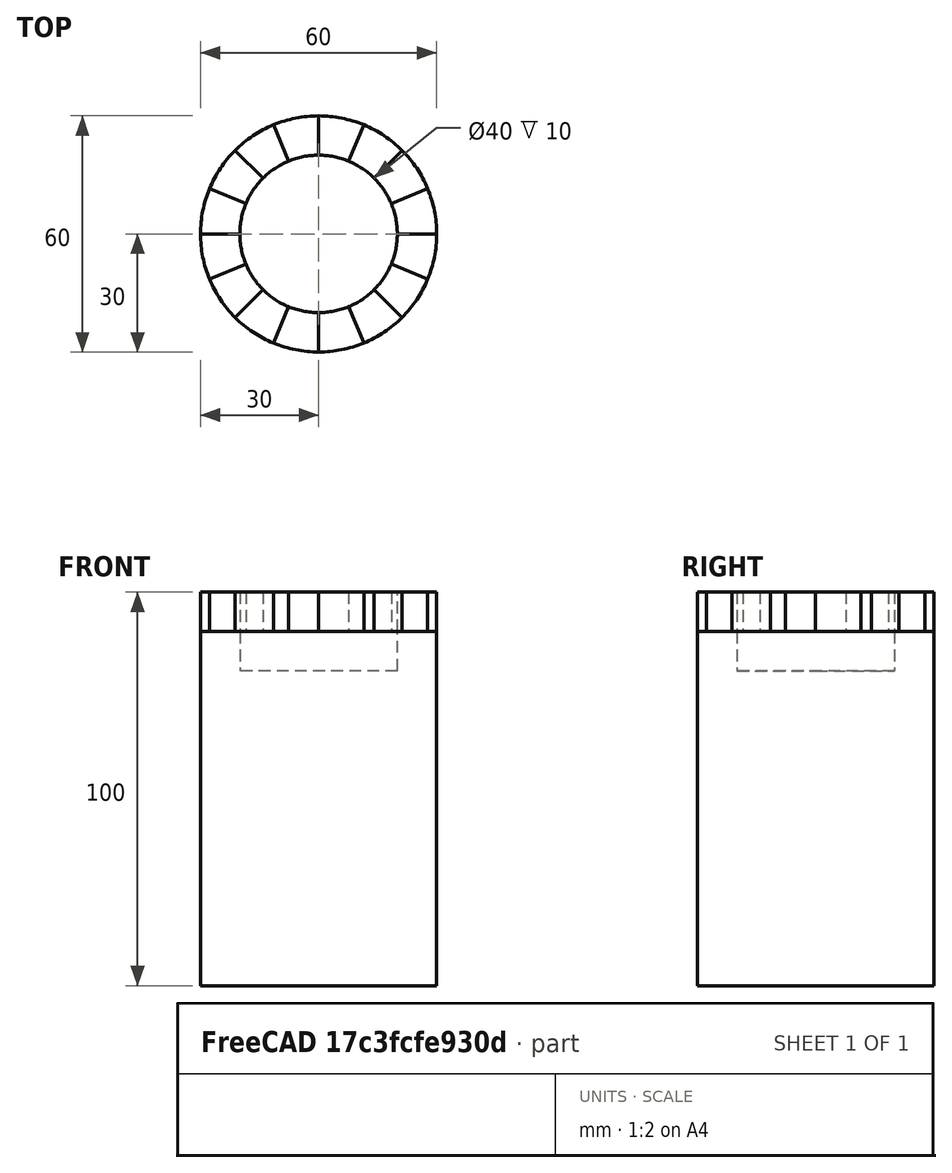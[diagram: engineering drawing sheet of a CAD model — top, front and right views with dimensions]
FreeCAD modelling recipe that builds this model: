
FCSTD DOCUMENT  (FreeCAD 0.21R33694 (Git))
Label: OJT1_T11R03_castillo
License: All rights reserved
LicenseURL: http://en.wikipedia.org/wiki/All_rights_reserved
objects: Part::Cylinder×11, Part::Cut×9
note: 20 computed .brp shape members not serialized (recipe doc carries the construction recipe); baked Part::Feature solids carry a one-line shape summary decoded from their .brp

FEATURE [Part::Cylinder] Cylinder
  Angle = 360
  AttacherType = Attacher::AttachEngine3D
  FirstAngle = 0
  Height = 90
  Radius = 30
  SecondAngle = 0
FEATURE [Part::Cylinder] Cylinder001
  Angle = 360
  AttacherType = Attacher::AttachEngine3D
  FirstAngle = 0
  Height = 10
  Placement = pos=(0,0,80) rot=(0,0,1;0rad)
  Radius = 20
  SecondAngle = 0
FEATURE [Part::Cut] Cut
  Base = -> Cylinder
  Refine = true
  Tool = -> Cylinder001
FEATURE [Part::Cylinder] Cylinder002
  Angle = 22.5
  AttacherType = Attacher::AttachEngine3D
  FirstAngle = 0
  Height = 10
  Placement = pos=(0,0,90) rot=(0,0,1;0rad)
  Radius = 30
  SecondAngle = 0
FEATURE [Part::Cylinder] Cylinder003
  Angle = 22.5
  AttacherType = Attacher::AttachEngine3D
  FirstAngle = 0
  Height = 10
  Placement = pos=(0,0,90) rot=(0,0,1;0.785398rad)
  Radius = 30
  SecondAngle = 0
FEATURE [Part::Cylinder] Cylinder004
  Angle = 22.5
  AttacherType = Attacher::AttachEngine3D
  FirstAngle = 0
  Height = 10
  Placement = pos=(0,0,90) rot=(0,0,1;1.5708rad)
  Radius = 30
  SecondAngle = 0
FEATURE [Part::Cylinder] Cylinder005
  Angle = 22.5
  AttacherType = Attacher::AttachEngine3D
  FirstAngle = 0
  Height = 10
  Placement = pos=(0,0,90) rot=(0,0,1;2.35619rad)
  Radius = 30
  SecondAngle = 0
FEATURE [Part::Cylinder] Cylinder006
  Angle = 22.5
  AttacherType = Attacher::AttachEngine3D
  FirstAngle = 0
  Height = 10
  Placement = pos=(0,0,90) rot=(0,0,1;3.14159rad)
  Radius = 30
  SecondAngle = 0
FEATURE [Part::Cylinder] Cylinder007
  Angle = 22.5
  AttacherType = Attacher::AttachEngine3D
  FirstAngle = 0
  Height = 10
  Placement = pos=(0,0,90) rot=(0,0,1;3.92699rad)
  Radius = 30
  SecondAngle = 0
FEATURE [Part::Cylinder] Cylinder008
  Angle = 22.5
  AttacherType = Attacher::AttachEngine3D
  FirstAngle = 0
  Height = 10
  Placement = pos=(0,0,90) rot=(0,0,1;4.71239rad)
  Radius = 30
  SecondAngle = 0
FEATURE [Part::Cylinder] Cylinder009
  Angle = 22.5
  AttacherType = Attacher::AttachEngine3D
  FirstAngle = 0
  Height = 10
  Placement = pos=(0,0,90) rot=(0,0,1;5.49779rad)
  Radius = 30
  SecondAngle = 0
FEATURE [Part::Cylinder] Cylinder010
  Angle = 360
  AttacherType = Attacher::AttachEngine3D
  FirstAngle = 0
  Height = 10
  Placement = pos=(0,0,90) rot=(0,0,1;0rad)
  Radius = 20
  SecondAngle = 0
FEATURE [Part::Cut] Cut001
  Base = -> Cylinder009
  Refine = true
  Tool = -> Cylinder010
FEATURE [Part::Cut] Cut002
  Base = -> Cylinder008
  Refine = true
  Tool = -> Cylinder010
FEATURE [Part::Cut] Cut003
  Base = -> Cylinder007
  Refine = true
  Tool = -> Cylinder010
FEATURE [Part::Cut] Cut004
  Base = -> Cylinder006
  Refine = true
  Tool = -> Cylinder010
FEATURE [Part::Cut] Cut005
  Base = -> Cylinder005
  Refine = true
  Tool = -> Cylinder010
FEATURE [Part::Cut] Cut006
  Base = -> Cylinder004
  Refine = true
  Tool = -> Cylinder010
FEATURE [Part::Cut] Cut007
  Base = -> Cylinder003
  Refine = true
  Tool = -> Cylinder010
FEATURE [Part::Cut] Cut008
  Base = -> Cylinder002
  Refine = true
  Tool = -> Cylinder010
